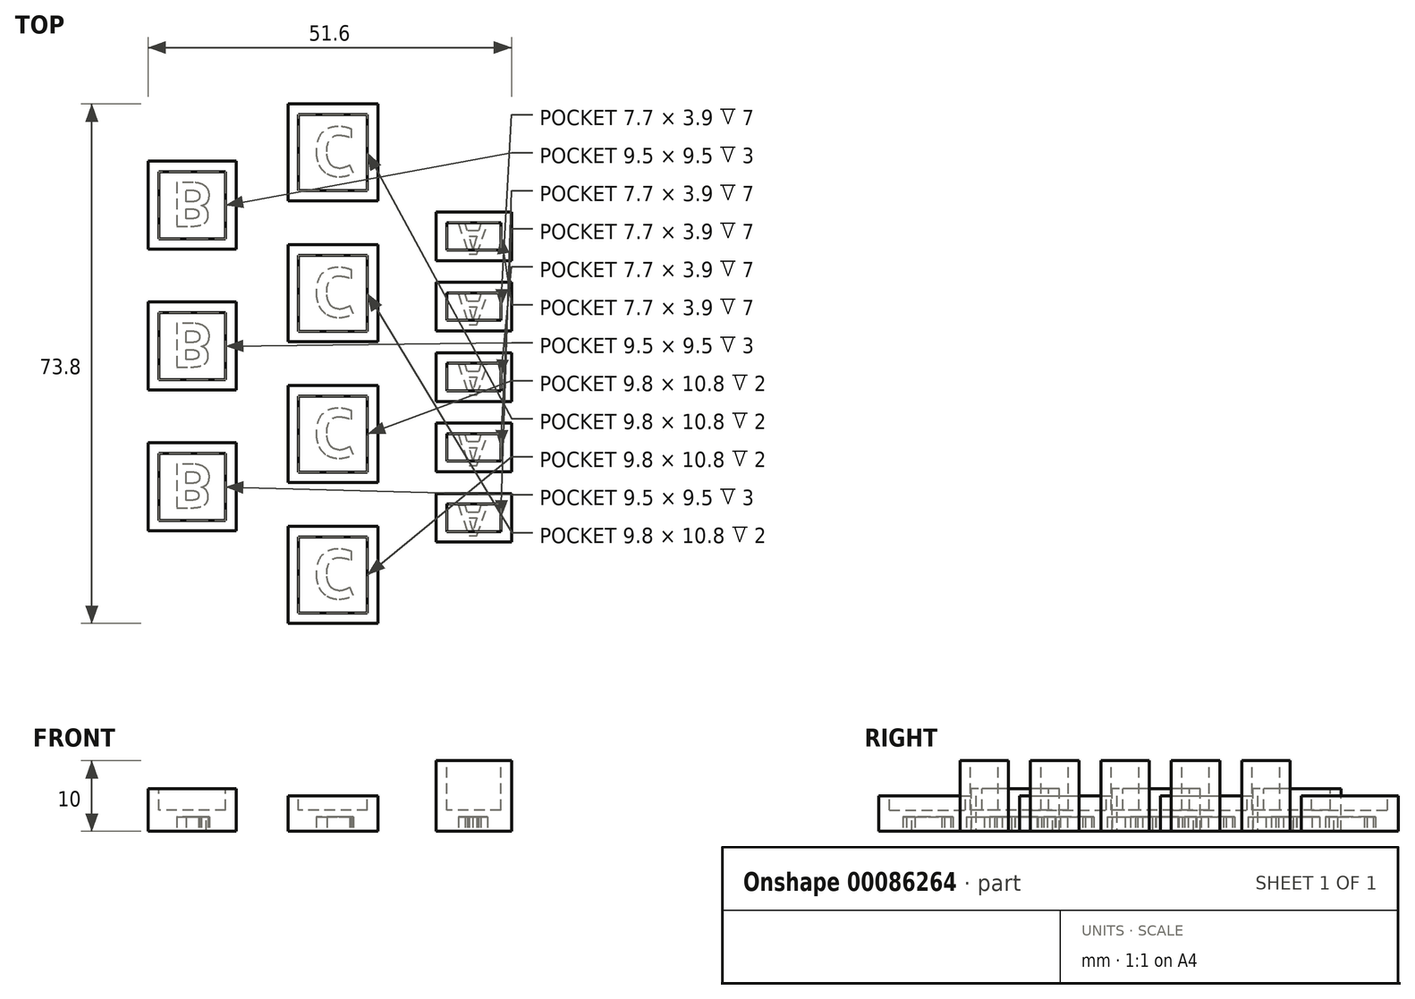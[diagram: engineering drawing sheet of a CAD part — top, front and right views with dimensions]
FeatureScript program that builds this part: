
annotation { "Feature Type Name" : "Feature", "Feature Type Description" : "" }
export const myFeature = defineFeature(function(context is Context, id is Id, definition is map)
    precondition{}
    {
        {
            var Q0;
            Q0=qCreatedBy(makeId("Top.planeOp"),FACE);
            var sketch = newSketch(context, id + "F0", { "sketchPlane" : qUnion([Q0])});
            skLineSegment(sketch, "E0.bottom", {"start": v(5.35, -3.45) * mm, "end": v(-5.35, -3.45) * mm});
            skLineSegment(sketch, "E0.top", {"start": v(5.35, 3.45) * mm, "end": v(-5.35, 3.45) * mm});
            skLineSegment(sketch, "E0.left", {"start": v(5.35, -3.45) * mm, "end": v(5.35, 3.45) * mm});
            skLineSegment(sketch, "E0.right", {"start": v(-5.35, -3.45) * mm, "end": v(-5.35, 3.45) * mm});
            skPoint(sketch, "E0.middle", {"position": v(0, 0) * mm});
            skSolve(sketch);
        }
        {
            var Q0;
            Q0 = qSketchRegion(id + "F0", true);
            extrude(context, id + "F1", {"entities" : qUnion([Q0]), "depth" : 10 * mm});
        }
        {
            var Q0;
            Q0=qCreatedBy(makeId("Top.planeOp"),FACE);
            var sketch = newSketch(context, id + "F2", { "sketchPlane" : qUnion([Q0])});
            skLineSegment(sketch, "E1.bottom", {"start": v(3.85, -1.95) * mm, "end": v(-3.85, -1.95) * mm});
            skLineSegment(sketch, "E1.top", {"start": v(3.85, 1.95) * mm, "end": v(-3.85, 1.95) * mm});
            skLineSegment(sketch, "E1.left", {"start": v(3.85, -1.95) * mm, "end": v(3.85, 1.95) * mm});
            skLineSegment(sketch, "E1.right", {"start": v(-3.85, -1.95) * mm, "end": v(-3.85, 1.95) * mm});
            skPoint(sketch, "E1.middle", {"position": v(0, 0) * mm});
            skSolve(sketch);
        }
        {
            var Q0;
            Q0 = qSketchRegion(id + "F2", true);
            extrude(context, id + "F3", {"entities" : qUnion([Q0]), "depth" : 7 * mm});
        }
        {
            var Q0;
            Q0=makeQuery(id+"F3.opExtrude","SWEPT_BODY",BODY,{"disambiguationData":[OSD([sQuery(id+"F2.wireOp",EDGE,"E1.bottom"),sQuery(id+"F2.wireOp",EDGE,"E1.top"),sQuery(id+"F2.wireOp",EDGE,"E1.left"),sQuery(id+"F2.wireOp",EDGE,"E1.right")])]});
            var Q1;
            Q1=makeQuery(id+"F1.opExtrude","SWEPT_BODY",BODY,{"disambiguationData":[OSD([sQuery(id+"F0.wireOp",EDGE,"E0.bottom"),sQuery(id+"F0.wireOp",EDGE,"E0.top"),sQuery(id+"F0.wireOp",EDGE,"E0.left"),sQuery(id+"F0.wireOp",EDGE,"E0.right")])]});
            booleanBodies(context, id + "F4", {"operationType" : BooleanOperationType.SUBTRACTION, "tools" : qUnion([Q0]), "targets" : qUnion([Q1])});
        }
        {
            var Q0;
            Q0=makeQuery(id+"F1.opExtrude","SWEPT_BODY",BODY,{"disambiguationData":[OSD([sQuery(id+"F0.wireOp",EDGE,"E0.bottom"),sQuery(id+"F0.wireOp",EDGE,"E0.top"),sQuery(id+"F0.wireOp",EDGE,"E0.left"),sQuery(id+"F0.wireOp",EDGE,"E0.right")])]});
            transform(context, id + "F5", {"entities" : qUnion([Q0]), "transformType" : TransformType.TRANSLATION_3D, "dx" : 20 * mm, "dy" : 0 * mm, "dz" : 0 * mm, "makeCopy" : false});
        }
        {
            var Q0;
            Q0=makeQuery(id+"F1.opExtrude","CAP_FACE",FACE,{"disambiguationData":[OSD([sQuery(id+"F0.wireOp",EDGE,"E0.bottom"),sQuery(id+"F0.wireOp",EDGE,"E0.top"),sQuery(id+"F0.wireOp",EDGE,"E0.left"),sQuery(id+"F0.wireOp",EDGE,"E0.right")])],"isStart":false});
            var sketch = newSketch(context, id + "F6", { "sketchPlane" : qUnion([Q0])});
            skText(sketch, "E2", { "text": "A", "fontName": "OpenSans-Bold.ttf"});
            const initialGuessF6  = {"E2": [0.0198, -0.0018, 1, 0, 0.00435]};
            skSetInitialGuess(sketch, initialGuessF6);
            skSolve(sketch);
        }
        {
            var Q0;
            Q0 = qSketchRegion(id + "F6", true);
            extrude(context, id + "F7", {"entities" : qUnion([Q0]), "oppositeDirection" : true, "depth" : 2 * mm});
        }
        {
            var Q0;
            Q0=makeQuery(id+"F7.opExtrude","SWEPT_BODY",BODY,{"disambiguationData":[OSD([sQuery(id+"F6.wireOp",EDGE,"E2.sketch_text.stroke-0"),sQuery(id+"F6.wireOp",EDGE,"E2.sketch_text.stroke-1"),sQuery(id+"F6.wireOp",EDGE,"E2.sketch_text.stroke-2"),sQuery(id+"F6.wireOp",EDGE,"E2.sketch_text.stroke-3"),sQuery(id+"F6.wireOp",EDGE,"E2.sketch_text.stroke-4"),sQuery(id+"F6.wireOp",EDGE,"E2.sketch_text.stroke-5"),sQuery(id+"F6.wireOp",EDGE,"E2.sketch_text.stroke-6"),sQuery(id+"F6.wireOp",EDGE,"E2.sketch_text.stroke-7"),sQuery(id+"F6.wireOp",EDGE,"E2.sketch_text.stroke-8"),sQuery(id+"F6.wireOp",EDGE,"E2.sketch_text.stroke-9"),sQuery(id+"F6.wireOp",EDGE,"E2.sketch_text.stroke-10"),sQuery(id+"F6.wireOp",EDGE,"E2.sketch_text.stroke-11")])]});
            transform(context, id + "F8", {"entities" : qUnion([Q0]), "transformType" : TransformType.TRANSLATION_3D, "dx" : -2 * mm, "dy" : 0 * mm, "dz" : 0 * mm, "makeCopy" : false});
        }
        {
            var Q0;
            Q0=makeQuery(id+"F7.opExtrude","SWEPT_BODY",BODY,{"disambiguationData":[OSD([sQuery(id+"F6.wireOp",EDGE,"E2.sketch_text.stroke-0"),sQuery(id+"F6.wireOp",EDGE,"E2.sketch_text.stroke-1"),sQuery(id+"F6.wireOp",EDGE,"E2.sketch_text.stroke-2"),sQuery(id+"F6.wireOp",EDGE,"E2.sketch_text.stroke-3"),sQuery(id+"F6.wireOp",EDGE,"E2.sketch_text.stroke-4"),sQuery(id+"F6.wireOp",EDGE,"E2.sketch_text.stroke-5"),sQuery(id+"F6.wireOp",EDGE,"E2.sketch_text.stroke-6"),sQuery(id+"F6.wireOp",EDGE,"E2.sketch_text.stroke-7"),sQuery(id+"F6.wireOp",EDGE,"E2.sketch_text.stroke-8"),sQuery(id+"F6.wireOp",EDGE,"E2.sketch_text.stroke-9"),sQuery(id+"F6.wireOp",EDGE,"E2.sketch_text.stroke-10"),sQuery(id+"F6.wireOp",EDGE,"E2.sketch_text.stroke-11")])]});
            var Q1;
            Q1=makeQuery(id+"F1.opExtrude","SWEPT_BODY",BODY,{"disambiguationData":[OSD([sQuery(id+"F0.wireOp",EDGE,"E0.bottom"),sQuery(id+"F0.wireOp",EDGE,"E0.top"),sQuery(id+"F0.wireOp",EDGE,"E0.left"),sQuery(id+"F0.wireOp",EDGE,"E0.right")])]});
            booleanBodies(context, id + "F9", {"operationType" : BooleanOperationType.SUBTRACTION, "tools" : qUnion([Q0]), "targets" : qUnion([Q1])});
        }
        {
            var Q0;
            Q0=qCreatedBy(makeId("Top.planeOp"),FACE);
            var sketch = newSketch(context, id + "F10", { "sketchPlane" : qUnion([Q0])});
            skLineSegment(sketch, "E3.bottom", {"start": v(-6.25, -6.25) * mm, "end": v(6.25, -6.25) * mm});
            skLineSegment(sketch, "E3.top", {"start": v(-6.25, 6.25) * mm, "end": v(6.25, 6.25) * mm});
            skLineSegment(sketch, "E3.left", {"start": v(-6.25, -6.25) * mm, "end": v(-6.25, 6.25) * mm});
            skLineSegment(sketch, "E3.right", {"start": v(6.25, -6.25) * mm, "end": v(6.25, 6.25) * mm});
            skPoint(sketch, "E3.middle", {"position": v(0, 0) * mm});
            skSolve(sketch);
        }
        {
            var Q0;
            Q0 = qSketchRegion(id + "F10", true);
            extrude(context, id + "F11", {"entities" : qUnion([Q0]), "depth" : 6 * mm});
        }
        {
            var Q0;
            Q0=qCreatedBy(makeId("Top.planeOp"),FACE);
            var sketch = newSketch(context, id + "F12", { "sketchPlane" : qUnion([Q0])});
            skLineSegment(sketch, "E4.bottom", {"start": v(4.75, -4.75) * mm, "end": v(-4.75, -4.75) * mm});
            skLineSegment(sketch, "E4.top", {"start": v(4.75, 4.75) * mm, "end": v(-4.75, 4.75) * mm});
            skLineSegment(sketch, "E4.left", {"start": v(4.75, -4.75) * mm, "end": v(4.75, 4.75) * mm});
            skLineSegment(sketch, "E4.right", {"start": v(-4.75, -4.75) * mm, "end": v(-4.75, 4.75) * mm});
            skPoint(sketch, "E4.middle", {"position": v(0, 0) * mm});
            skSolve(sketch);
        }
        {
            var Q0;
            Q0 = qSketchRegion(id + "F12", true);
            extrude(context, id + "F13", {"entities" : qUnion([Q0]), "depth" : 3 * mm});
        }
        {
            var Q0;
            Q0=makeQuery(id+"F13.opExtrude","SWEPT_BODY",BODY,{"disambiguationData":[OSD([sQuery(id+"F12.wireOp",EDGE,"E4.bottom"),sQuery(id+"F12.wireOp",EDGE,"E4.top"),sQuery(id+"F12.wireOp",EDGE,"E4.left"),sQuery(id+"F12.wireOp",EDGE,"E4.right")])]});
            var Q1;
            Q1=makeQuery(id+"F11.opExtrude","SWEPT_BODY",BODY,{"disambiguationData":[OSD([sQuery(id+"F10.wireOp",EDGE,"E3.bottom"),sQuery(id+"F10.wireOp",EDGE,"E3.top"),sQuery(id+"F10.wireOp",EDGE,"E3.left"),sQuery(id+"F10.wireOp",EDGE,"E3.right")])]});
            booleanBodies(context, id + "F14", {"operationType" : BooleanOperationType.SUBTRACTION, "tools" : qUnion([Q0]), "targets" : qUnion([Q1])});
        }
        {
            var Q0;
            Q0=makeQuery(id+"F11.opExtrude","CAP_FACE",FACE,{"disambiguationData":[OSD([sQuery(id+"F10.wireOp",EDGE,"E3.bottom"),sQuery(id+"F10.wireOp",EDGE,"E3.top"),sQuery(id+"F10.wireOp",EDGE,"E3.left"),sQuery(id+"F10.wireOp",EDGE,"E3.right")])],"isStart":false});
            var sketch = newSketch(context, id + "F15", { "sketchPlane" : qUnion([Q0])});
            skText(sketch, "E5", { "text": "B", "fontName": "OpenSans-Bold.ttf"});
            const initialGuessF15  = {"E5": [-0.00294, -0.00322, 1, 0, 0.00625]};
            skSetInitialGuess(sketch, initialGuessF15);
            skSolve(sketch);
        }
        {
            var Q0;
            Q0 = qSketchRegion(id + "F15", true);
            extrude(context, id + "F16", {"entities" : qUnion([Q0]), "oppositeDirection" : true, "depth" : 2 * mm});
        }
        {
            var Q0;
            Q0=makeQuery(id+"F16.opExtrude","SWEPT_BODY",BODY,{"disambiguationData":[OSD([sQuery(id+"F15.wireOp",EDGE,"E5.sketch_text.stroke-0"),sQuery(id+"F15.wireOp",EDGE,"E5.sketch_text.stroke-1"),sQuery(id+"F15.wireOp",EDGE,"E5.sketch_text.stroke-2"),sQuery(id+"F15.wireOp",EDGE,"E5.sketch_text.stroke-3"),sQuery(id+"F15.wireOp",EDGE,"E5.sketch_text.stroke-4"),sQuery(id+"F15.wireOp",EDGE,"E5.sketch_text.stroke-5"),sQuery(id+"F15.wireOp",EDGE,"E5.sketch_text.stroke-6"),sQuery(id+"F15.wireOp",EDGE,"E5.sketch_text.stroke-7"),sQuery(id+"F15.wireOp",EDGE,"E5.sketch_text.stroke-8"),sQuery(id+"F15.wireOp",EDGE,"E5.sketch_text.stroke-9"),sQuery(id+"F15.wireOp",EDGE,"E5.sketch_text.stroke-10"),sQuery(id+"F15.wireOp",EDGE,"E5.sketch_text.stroke-11"),sQuery(id+"F15.wireOp",EDGE,"E5.sketch_text.stroke-12"),sQuery(id+"F15.wireOp",EDGE,"E5.sketch_text.stroke-13"),sQuery(id+"F15.wireOp",EDGE,"E5.sketch_text.stroke-14"),sQuery(id+"F15.wireOp",EDGE,"E5.sketch_text.stroke-15"),sQuery(id+"F15.wireOp",EDGE,"E5.sketch_text.stroke-16"),sQuery(id+"F15.wireOp",EDGE,"E5.sketch_text.stroke-17"),sQuery(id+"F15.wireOp",EDGE,"E5.sketch_text.stroke-18"),sQuery(id+"F15.wireOp",EDGE,"E5.sketch_text.stroke-19"),sQuery(id+"F15.wireOp",EDGE,"E5.sketch_text.stroke-20"),sQuery(id+"F15.wireOp",EDGE,"E5.sketch_text.stroke-21"),sQuery(id+"F15.wireOp",EDGE,"E5.sketch_text.stroke-22"),sQuery(id+"F15.wireOp",EDGE,"E5.sketch_text.stroke-23"),sQuery(id+"F15.wireOp",EDGE,"E5.sketch_text.stroke-24")])]});
            var Q1;
            Q1=makeQuery(id+"F11.opExtrude","SWEPT_BODY",BODY,{"disambiguationData":[OSD([sQuery(id+"F10.wireOp",EDGE,"E3.bottom"),sQuery(id+"F10.wireOp",EDGE,"E3.top"),sQuery(id+"F10.wireOp",EDGE,"E3.left"),sQuery(id+"F10.wireOp",EDGE,"E3.right")])]});
            booleanBodies(context, id + "F17", {"operationType" : BooleanOperationType.SUBTRACTION, "tools" : qUnion([Q0]), "targets" : qUnion([Q1])});
        }
        {
            var Q0;
            Q0=makeQuery(id+"F1.opExtrude","SWEPT_BODY",BODY,{"disambiguationData":[OSD([sQuery(id+"F0.wireOp",EDGE,"E0.bottom"),sQuery(id+"F0.wireOp",EDGE,"E0.top"),sQuery(id+"F0.wireOp",EDGE,"E0.left"),sQuery(id+"F0.wireOp",EDGE,"E0.right")])]});
            var Q1;
            Q1=makeQuery(id+"F1.opExtrude","CAP_EDGE",EDGE,{"disambiguationData":[OSD([sQuery(id+"F0.wireOp",EDGE,"E0.bottom")])],"isStart":true});
            transform(context, id + "F18", {"entities" : qUnion([Q0]), "transformType" : TransformType.ROTATION, "transformAxis" : qUnion([Q1]), "angle" : 180 * degree, "makeCopy" : false});
        }
        {
            var Q0;
            Q0=makeQuery(id+"F11.opExtrude","SWEPT_BODY",BODY,{"disambiguationData":[OSD([sQuery(id+"F10.wireOp",EDGE,"E3.bottom"),sQuery(id+"F10.wireOp",EDGE,"E3.top"),sQuery(id+"F10.wireOp",EDGE,"E3.left"),sQuery(id+"F10.wireOp",EDGE,"E3.right")])]});
            var Q1;
            Q1=makeQuery(id+"F11.opExtrude","CAP_EDGE",EDGE,{"disambiguationData":[OSD([sQuery(id+"F10.wireOp",EDGE,"E3.bottom")])],"isStart":true});
            transform(context, id + "F19", {"entities" : qUnion([Q0]), "transformType" : TransformType.ROTATION, "transformAxis" : qUnion([Q1]), "angle" : 180 * degree, "makeCopy" : false});
        }
        {
            var Q0;
            Q0=makeQuery(id+"F11.opExtrude","SWEPT_BODY",BODY,{"disambiguationData":[OSD([sQuery(id+"F10.wireOp",EDGE,"E3.bottom"),sQuery(id+"F10.wireOp",EDGE,"E3.top"),sQuery(id+"F10.wireOp",EDGE,"E3.left"),sQuery(id+"F10.wireOp",EDGE,"E3.right")])]});
            transform(context, id + "F20", {"entities" : qUnion([Q0]), "transformType" : TransformType.TRANSLATION_3D, "dx" : 0 * mm, "dy" : 0 * mm, "dz" : 6 * mm, "makeCopy" : false});
        }
        {
            var Q0;
            Q0=makeQuery(id+"F1.opExtrude","SWEPT_BODY",BODY,{"disambiguationData":[OSD([sQuery(id+"F0.wireOp",EDGE,"E0.bottom"),sQuery(id+"F0.wireOp",EDGE,"E0.top"),sQuery(id+"F0.wireOp",EDGE,"E0.left"),sQuery(id+"F0.wireOp",EDGE,"E0.right")])]});
            transform(context, id + "F21", {"entities" : qUnion([Q0]), "transformType" : TransformType.TRANSLATION_3D, "dx" : 0 * mm, "dy" : 0 * mm, "dz" : 10 * mm, "makeCopy" : false});
        }
        {
            var Q0;
            Q0=makeQuery(id+"F1.opExtrude","SWEPT_BODY",BODY,{"disambiguationData":[OSD([sQuery(id+"F0.wireOp",EDGE,"E0.bottom"),sQuery(id+"F0.wireOp",EDGE,"E0.top"),sQuery(id+"F0.wireOp",EDGE,"E0.left"),sQuery(id+"F0.wireOp",EDGE,"E0.right")])]});
            transform(context, id + "F22", {"entities" : qUnion([Q0]), "transformType" : TransformType.TRANSLATION_3D, "dx" : 0 * mm, "dy" : 10 * mm, "dz" : 0 * mm, "makeCopy" : true});
        }
        {
            var Q0;
            Q0=makeQuery(id+"F1.opExtrude","SWEPT_BODY",BODY,{"disambiguationData":[OSD([sQuery(id+"F0.wireOp",EDGE,"E0.bottom"),sQuery(id+"F0.wireOp",EDGE,"E0.top"),sQuery(id+"F0.wireOp",EDGE,"E0.left"),sQuery(id+"F0.wireOp",EDGE,"E0.right")])]});
            transform(context, id + "F23", {"entities" : qUnion([Q0]), "transformType" : TransformType.TRANSLATION_3D, "dx" : 0 * mm, "dy" : -10 * mm, "dz" : 0 * mm, "makeCopy" : true});
        }
        {
            var Q0;
            Q0=makeQuery(id+"F23.opPattern","COPY",BODY,{"derivedFrom":makeQuery(id+"F1.opExtrude","SWEPT_BODY",BODY,{"disambiguationData":[OSD([sQuery(id+"F0.wireOp",EDGE,"E0.bottom"),sQuery(id+"F0.wireOp",EDGE,"E0.top"),sQuery(id+"F0.wireOp",EDGE,"E0.left"),sQuery(id+"F0.wireOp",EDGE,"E0.right")])]}),"instanceName":"1"});
            transform(context, id + "F24", {"entities" : qUnion([Q0]), "transformType" : TransformType.TRANSLATION_3D, "dx" : 0 * mm, "dy" : 0 * mm, "dz" : -10 * mm, "makeCopy" : false});
        }
        {
            var Q0;
            Q0=makeQuery(id+"F23.opPattern","COPY",BODY,{"derivedFrom":makeQuery(id+"F1.opExtrude","SWEPT_BODY",BODY,{"disambiguationData":[OSD([sQuery(id+"F0.wireOp",EDGE,"E0.bottom"),sQuery(id+"F0.wireOp",EDGE,"E0.top"),sQuery(id+"F0.wireOp",EDGE,"E0.left"),sQuery(id+"F0.wireOp",EDGE,"E0.right")])]}),"instanceName":"1"});
            transform(context, id + "F25", {"entities" : qUnion([Q0]), "transformType" : TransformType.TRANSLATION_3D, "dx" : 0 * mm, "dy" : -10 * mm, "dz" : 0 * mm, "makeCopy" : true});
        }
        {
            var Q0;
            Q0=makeQuery(id+"F22.opPattern","COPY",BODY,{"derivedFrom":makeQuery(id+"F1.opExtrude","SWEPT_BODY",BODY,{"disambiguationData":[OSD([sQuery(id+"F0.wireOp",EDGE,"E0.bottom"),sQuery(id+"F0.wireOp",EDGE,"E0.top"),sQuery(id+"F0.wireOp",EDGE,"E0.left"),sQuery(id+"F0.wireOp",EDGE,"E0.right")])]}),"instanceName":"1"});
            transform(context, id + "F26", {"entities" : qUnion([Q0]), "transformType" : TransformType.TRANSLATION_3D, "dx" : 0 * mm, "dy" : 10 * mm, "dz" : 0 * mm, "makeCopy" : false});
        }
        {
            var Q0;
            Q0=makeQuery(id+"F22.opPattern","COPY",BODY,{"derivedFrom":makeQuery(id+"F1.opExtrude","SWEPT_BODY",BODY,{"disambiguationData":[OSD([sQuery(id+"F0.wireOp",EDGE,"E0.bottom"),sQuery(id+"F0.wireOp",EDGE,"E0.top"),sQuery(id+"F0.wireOp",EDGE,"E0.left"),sQuery(id+"F0.wireOp",EDGE,"E0.right")])]}),"instanceName":"1"});
            transform(context, id + "F27", {"entities" : qUnion([Q0]), "transformType" : TransformType.TRANSLATION_3D, "dx" : 0 * mm, "dy" : -10 * mm, "dz" : 0 * mm, "makeCopy" : true});
        }
        {
            var Q0;
            Q0=makeQuery(id+"F11.opExtrude","SWEPT_BODY",BODY,{"disambiguationData":[OSD([sQuery(id+"F10.wireOp",EDGE,"E3.bottom"),sQuery(id+"F10.wireOp",EDGE,"E3.top"),sQuery(id+"F10.wireOp",EDGE,"E3.left"),sQuery(id+"F10.wireOp",EDGE,"E3.right")])]});
            transform(context, id + "F28", {"entities" : qUnion([Q0]), "transformType" : TransformType.TRANSLATION_3D, "dx" : 0 * mm, "dy" : 20 * mm, "dz" : 0 * mm, "makeCopy" : true});
        }
        {
            var Q0;
            Q0=makeQuery(id+"F11.opExtrude","SWEPT_BODY",BODY,{"disambiguationData":[OSD([sQuery(id+"F10.wireOp",EDGE,"E3.bottom"),sQuery(id+"F10.wireOp",EDGE,"E3.top"),sQuery(id+"F10.wireOp",EDGE,"E3.left"),sQuery(id+"F10.wireOp",EDGE,"E3.right")])]});
            transform(context, id + "F29", {"entities" : qUnion([Q0]), "transformType" : TransformType.TRANSLATION_3D, "dx" : 0 * mm, "dy" : -20 * mm, "dz" : 0 * mm, "makeCopy" : true});
        }
        {
            var Q0;
            Q0=makeQuery(id+"F29.opPattern","COPY",BODY,{"derivedFrom":makeQuery(id+"F11.opExtrude","SWEPT_BODY",BODY,{"disambiguationData":[OSD([sQuery(id+"F10.wireOp",EDGE,"E3.bottom"),sQuery(id+"F10.wireOp",EDGE,"E3.top"),sQuery(id+"F10.wireOp",EDGE,"E3.left"),sQuery(id+"F10.wireOp",EDGE,"E3.right")])]}),"instanceName":"1"});
            var Q1;
            Q1=makeQuery(id+"F28.opPattern","COPY",BODY,{"derivedFrom":makeQuery(id+"F11.opExtrude","SWEPT_BODY",BODY,{"disambiguationData":[OSD([sQuery(id+"F10.wireOp",EDGE,"E3.bottom"),sQuery(id+"F10.wireOp",EDGE,"E3.top"),sQuery(id+"F10.wireOp",EDGE,"E3.left"),sQuery(id+"F10.wireOp",EDGE,"E3.right")])]}),"instanceName":"1"});
            var Q2;
            Q2=makeQuery(id+"F11.opExtrude","SWEPT_BODY",BODY,{"disambiguationData":[OSD([sQuery(id+"F10.wireOp",EDGE,"E3.bottom"),sQuery(id+"F10.wireOp",EDGE,"E3.top"),sQuery(id+"F10.wireOp",EDGE,"E3.left"),sQuery(id+"F10.wireOp",EDGE,"E3.right")])]});
            transform(context, id + "F30", {"entities" : qUnion([Q0, Q1, Q2]), "transformType" : TransformType.TRANSLATION_3D, "dx" : -20 * mm, "dy" : 10 * mm, "dz" : 0 * mm, "makeCopy" : false});
        }
        {
            var Q0;
            Q0=qCreatedBy(makeId("Top.planeOp"),FACE);
            var sketch = newSketch(context, id + "F31", { "sketchPlane" : qUnion([Q0])});
            skLineSegment(sketch, "E6.bottom", {"start": v(6.4, -6.9) * mm, "end": v(-6.4, -6.9) * mm});
            skLineSegment(sketch, "E6.top", {"start": v(6.4, 6.9) * mm, "end": v(-6.4, 6.9) * mm});
            skLineSegment(sketch, "E6.left", {"start": v(6.4, -6.9) * mm, "end": v(6.4, 6.9) * mm});
            skLineSegment(sketch, "E6.right", {"start": v(-6.4, -6.9) * mm, "end": v(-6.4, 6.9) * mm});
            skPoint(sketch, "E6.middle", {"position": v(0, 0) * mm});
            skSolve(sketch);
        }
        {
            var Q0;
            Q0 = qSketchRegion(id + "F31", true);
            extrude(context, id + "F32", {"entities" : qUnion([Q0]), "depth" : 5 * mm});
        }
        {
            var Q0;
            Q0=makeQuery(id+"F32.opExtrude","CAP_FACE",FACE,{"disambiguationData":[OSD([sQuery(id+"F31.wireOp",EDGE,"E6.bottom"),sQuery(id+"F31.wireOp",EDGE,"E6.top"),sQuery(id+"F31.wireOp",EDGE,"E6.left"),sQuery(id+"F31.wireOp",EDGE,"E6.right")])],"isStart":false});
            var sketch = newSketch(context, id + "F33", { "sketchPlane" : qUnion([Q0])});
            skLineSegment(sketch, "E7.bottom", {"start": v(4.9, -5.4) * mm, "end": v(-4.9, -5.4) * mm});
            skLineSegment(sketch, "E7.top", {"start": v(4.9, 5.4) * mm, "end": v(-4.9, 5.4) * mm});
            skLineSegment(sketch, "E7.left", {"start": v(4.9, -5.4) * mm, "end": v(4.9, 5.4) * mm});
            skLineSegment(sketch, "E7.right", {"start": v(-4.9, -5.4) * mm, "end": v(-4.9, 5.4) * mm});
            skPoint(sketch, "E7.middle", {"position": v(0, 0) * mm});
            skSolve(sketch);
        }
        {
            var Q0;
            Q0 = qSketchRegion(id + "F33", true);
            extrude(context, id + "F34", {"entities" : qUnion([Q0]), "oppositeDirection" : true, "depth" : 2 * mm});
        }
        {
            var Q0;
            Q0=makeQuery(id+"F34.opExtrude","SWEPT_BODY",BODY,{"disambiguationData":[OSD([sQuery(id+"F33.wireOp",EDGE,"E7.bottom"),sQuery(id+"F33.wireOp",EDGE,"E7.top"),sQuery(id+"F33.wireOp",EDGE,"E7.left"),sQuery(id+"F33.wireOp",EDGE,"E7.right")])]});
            var Q1;
            Q1=makeQuery(id+"F32.opExtrude","SWEPT_BODY",BODY,{"disambiguationData":[OSD([sQuery(id+"F31.wireOp",EDGE,"E6.bottom"),sQuery(id+"F31.wireOp",EDGE,"E6.top"),sQuery(id+"F31.wireOp",EDGE,"E6.left"),sQuery(id+"F31.wireOp",EDGE,"E6.right")])]});
            booleanBodies(context, id + "F35", {"operationType" : BooleanOperationType.SUBTRACTION, "tools" : qUnion([Q0]), "targets" : qUnion([Q1])});
        }
        {
            var Q0;
            Q0=makeQuery(id+"F23.opPattern","COPY",BODY,{"derivedFrom":makeQuery(id+"F1.opExtrude","SWEPT_BODY",BODY,{"disambiguationData":[OSD([sQuery(id+"F0.wireOp",EDGE,"E0.bottom"),sQuery(id+"F0.wireOp",EDGE,"E0.top"),sQuery(id+"F0.wireOp",EDGE,"E0.left"),sQuery(id+"F0.wireOp",EDGE,"E0.right")])]}),"instanceName":"1"});
            var Q1;
            Q1=makeQuery(id+"F25.opPattern","COPY",BODY,{"derivedFrom":makeQuery(id+"F23.opPattern","COPY",BODY,{"derivedFrom":makeQuery(id+"F1.opExtrude","SWEPT_BODY",BODY,{"disambiguationData":[OSD([sQuery(id+"F0.wireOp",EDGE,"E0.bottom"),sQuery(id+"F0.wireOp",EDGE,"E0.top"),sQuery(id+"F0.wireOp",EDGE,"E0.left"),sQuery(id+"F0.wireOp",EDGE,"E0.right")])]}),"instanceName":"1"}),"instanceName":"1"});
            transform(context, id + "F36", {"entities" : qUnion([Q0, Q1]), "transformType" : TransformType.TRANSLATION_3D, "dx" : 0 * mm, "dy" : 0 * mm, "dz" : 10 * mm, "makeCopy" : false});
        }
        {
            var Q0;
            Q0=makeQuery(id+"F32.opExtrude","CAP_FACE",FACE,{"disambiguationData":[OSD([sQuery(id+"F31.wireOp",EDGE,"E6.bottom"),sQuery(id+"F31.wireOp",EDGE,"E6.top"),sQuery(id+"F31.wireOp",EDGE,"E6.left"),sQuery(id+"F31.wireOp",EDGE,"E6.right")])],"isStart":true});
            var sketch = newSketch(context, id + "F37", { "sketchPlane" : qUnion([Q0])});
            skText(sketch, "E8", { "text": "C", "fontName": "OpenSans-Bold.ttf"});
            const initialGuessF37  = {"E8": [-0.00294, -0.00358, 1, 0, 0.00698]};
            skSetInitialGuess(sketch, initialGuessF37);
            skSolve(sketch);
        }
        {
            var Q0;
            Q0 = qSketchRegion(id + "F37", true);
            extrude(context, id + "F38", {"entities" : qUnion([Q0]), "oppositeDirection" : true, "depth" : 2 * mm});
        }
        {
            var Q0;
            Q0=makeQuery(id+"F38.opExtrude","SWEPT_BODY",BODY,{"disambiguationData":[OSD([sQuery(id+"F37.wireOp",EDGE,"E8.sketch_text.stroke-0"),sQuery(id+"F37.wireOp",EDGE,"E8.sketch_text.stroke-1"),sQuery(id+"F37.wireOp",EDGE,"E8.sketch_text.stroke-2"),sQuery(id+"F37.wireOp",EDGE,"E8.sketch_text.stroke-3"),sQuery(id+"F37.wireOp",EDGE,"E8.sketch_text.stroke-4"),sQuery(id+"F37.wireOp",EDGE,"E8.sketch_text.stroke-5"),sQuery(id+"F37.wireOp",EDGE,"E8.sketch_text.stroke-6"),sQuery(id+"F37.wireOp",EDGE,"E8.sketch_text.stroke-7"),sQuery(id+"F37.wireOp",EDGE,"E8.sketch_text.stroke-8"),sQuery(id+"F37.wireOp",EDGE,"E8.sketch_text.stroke-9"),sQuery(id+"F37.wireOp",EDGE,"E8.sketch_text.stroke-10"),sQuery(id+"F37.wireOp",EDGE,"E8.sketch_text.stroke-11"),sQuery(id+"F37.wireOp",EDGE,"E8.sketch_text.stroke-12"),sQuery(id+"F37.wireOp",EDGE,"E8.sketch_text.stroke-13"),sQuery(id+"F37.wireOp",EDGE,"E8.sketch_text.stroke-14")])]});
            var Q1;
            Q1=makeQuery(id+"F32.opExtrude","SWEPT_BODY",BODY,{"disambiguationData":[OSD([sQuery(id+"F31.wireOp",EDGE,"E6.bottom"),sQuery(id+"F31.wireOp",EDGE,"E6.top"),sQuery(id+"F31.wireOp",EDGE,"E6.left"),sQuery(id+"F31.wireOp",EDGE,"E6.right")])]});
            booleanBodies(context, id + "F39", {"operationType" : BooleanOperationType.SUBTRACTION, "tools" : qUnion([Q0]), "targets" : qUnion([Q1])});
        }
        {
            var Q0;
            Q0=makeQuery(id+"F32.opExtrude","SWEPT_BODY",BODY,{"disambiguationData":[OSD([sQuery(id+"F31.wireOp",EDGE,"E6.bottom"),sQuery(id+"F31.wireOp",EDGE,"E6.top"),sQuery(id+"F31.wireOp",EDGE,"E6.left"),sQuery(id+"F31.wireOp",EDGE,"E6.right")])]});
            transform(context, id + "F40", {"entities" : qUnion([Q0]), "transformType" : TransformType.TRANSLATION_3D, "dx" : 0 * mm, "dy" : -20 * mm, "dz" : 0 * mm, "makeCopy" : true});
        }
        {
            var Q0;
            Q0=makeQuery(id+"F32.opExtrude","SWEPT_BODY",BODY,{"disambiguationData":[OSD([sQuery(id+"F31.wireOp",EDGE,"E6.bottom"),sQuery(id+"F31.wireOp",EDGE,"E6.top"),sQuery(id+"F31.wireOp",EDGE,"E6.left"),sQuery(id+"F31.wireOp",EDGE,"E6.right")])]});
            var Q1;
            Q1=makeQuery(id+"F40.opPattern","COPY",BODY,{"derivedFrom":makeQuery(id+"F32.opExtrude","SWEPT_BODY",BODY,{"disambiguationData":[OSD([sQuery(id+"F31.wireOp",EDGE,"E6.bottom"),sQuery(id+"F31.wireOp",EDGE,"E6.top"),sQuery(id+"F31.wireOp",EDGE,"E6.left"),sQuery(id+"F31.wireOp",EDGE,"E6.right")])]}),"instanceName":"1"});
            transform(context, id + "F41", {"entities" : qUnion([Q0, Q1]), "transformType" : TransformType.TRANSLATION_3D, "dx" : 0 * mm, "dy" : 40 * mm, "dz" : 0 * mm, "makeCopy" : true});
        }
        {
            var Q0;
            Q0=makeQuery(id+"F32.opExtrude","SWEPT_BODY",BODY,{"disambiguationData":[OSD([sQuery(id+"F31.wireOp",EDGE,"E6.bottom"),sQuery(id+"F31.wireOp",EDGE,"E6.top"),sQuery(id+"F31.wireOp",EDGE,"E6.left"),sQuery(id+"F31.wireOp",EDGE,"E6.right")])]});
            var Q1;
            Q1=makeQuery(id+"F40.opPattern","COPY",BODY,{"derivedFrom":makeQuery(id+"F32.opExtrude","SWEPT_BODY",BODY,{"disambiguationData":[OSD([sQuery(id+"F31.wireOp",EDGE,"E6.bottom"),sQuery(id+"F31.wireOp",EDGE,"E6.top"),sQuery(id+"F31.wireOp",EDGE,"E6.left"),sQuery(id+"F31.wireOp",EDGE,"E6.right")])]}),"instanceName":"1"});
            var Q2;
            Q2=makeQuery(id+"F41.opPattern","COPY",BODY,{"derivedFrom":makeQuery(id+"F32.opExtrude","SWEPT_BODY",BODY,{"disambiguationData":[OSD([sQuery(id+"F31.wireOp",EDGE,"E6.bottom"),sQuery(id+"F31.wireOp",EDGE,"E6.top"),sQuery(id+"F31.wireOp",EDGE,"E6.left"),sQuery(id+"F31.wireOp",EDGE,"E6.right")])]}),"instanceName":"1"});
            var Q3;
            Q3=makeQuery(id+"F41.opPattern","COPY",BODY,{"derivedFrom":makeQuery(id+"F40.opPattern","COPY",BODY,{"derivedFrom":makeQuery(id+"F32.opExtrude","SWEPT_BODY",BODY,{"disambiguationData":[OSD([sQuery(id+"F31.wireOp",EDGE,"E6.bottom"),sQuery(id+"F31.wireOp",EDGE,"E6.top"),sQuery(id+"F31.wireOp",EDGE,"E6.left"),sQuery(id+"F31.wireOp",EDGE,"E6.right")])]}),"instanceName":"1"}),"instanceName":"1"});
            transform(context, id + "F42", {"entities" : qUnion([Q0, Q1, Q2, Q3]), "transformType" : TransformType.TRANSLATION_3D, "dx" : 0 * mm, "dy" : -15 * mm, "dz" : 0 * mm, "makeCopy" : false});
        }
    });
